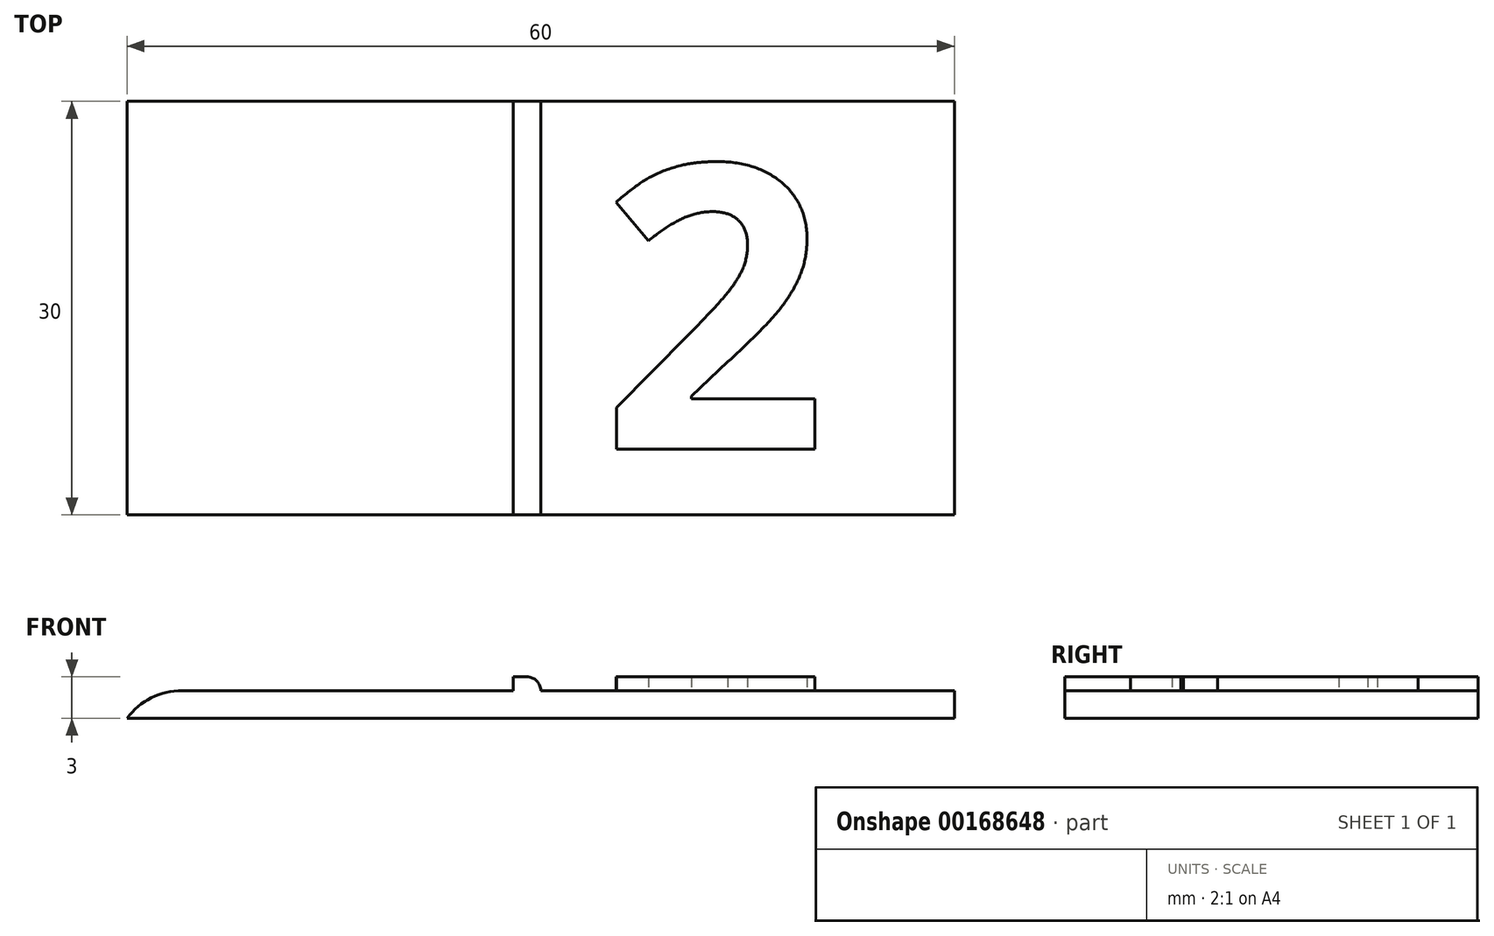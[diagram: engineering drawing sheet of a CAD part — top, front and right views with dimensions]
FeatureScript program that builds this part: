
annotation { "Feature Type Name" : "Feature", "Feature Type Description" : "" }
export const myFeature = defineFeature(function(context is Context, id is Id, definition is map)
    precondition{}
    {
        {
            var Q0;
            Q0=qCreatedBy(makeId("Top.planeOp"),FACE);
            var sketch = newSketch(context, id + "F0", { "sketchPlane" : qUnion([Q0])});
            skLineSegment(sketch, "E0.bottom", {"start": v(0, 0) * mm, "end": v(60, 0) * mm});
            skLineSegment(sketch, "E0.top", {"start": v(0, 30) * mm, "end": v(60, 30) * mm});
            skLineSegment(sketch, "E0.left", {"start": v(0, 0) * mm, "end": v(0, 30) * mm});
            skLineSegment(sketch, "E0.right", {"start": v(60, 0) * mm, "end": v(60, 30) * mm});
            skSolve(sketch);
        }
        {
            var Q0;
            Q0 = qSketchRegion(id + "F0", true);
            extrude(context, id + "F1", {"entities" : qUnion([Q0]), "depth" : 2 * mm});
        }
        {
            var Q0;
            Q0=makeQuery(id+"F1.opExtrude","CAP_FACE",FACE,{"disambiguationData":[OSD([sQuery(id+"F0.wireOp",EDGE,"E0.bottom"),sQuery(id+"F0.wireOp",EDGE,"E0.top"),sQuery(id+"F0.wireOp",EDGE,"E0.left"),sQuery(id+"F0.wireOp",EDGE,"E0.right")])],"isStart":false});
            var sketch = newSketch(context, id + "F2", { "sketchPlane" : qUnion([Q0])});
            skLineSegment(sketch, "E1.bottom", {"start": v(30, 30) * mm, "end": v(28, 30) * mm});
            skLineSegment(sketch, "E1.top", {"start": v(30, 0) * mm, "end": v(28, 0) * mm});
            skLineSegment(sketch, "E1.left", {"start": v(30, 30) * mm, "end": v(30, 0) * mm});
            skLineSegment(sketch, "E1.right", {"start": v(28, 30) * mm, "end": v(28, 0) * mm});
            skSolve(sketch);
        }
        {
            var Q0;
            Q0 = qSketchRegion(id + "F2", true);
            extrude(context, id + "F3", {"entities" : qUnion([Q0]), "operationType" : NewBodyOperationType.ADD, "depth" : 1 * mm});
        }
        {
            var Q0;
            Q0=makeQuery(id+"F3.opExtrude","CAP_EDGE",EDGE,{"disambiguationData":[OSD([sQuery(id+"F2.wireOp",EDGE,"E1.left")])],"isStart":false});
            fillet(context, id + "F4", {"entities" : qUnion([Q0]), "radius" : 1 * mm, "tangentPropagation" : true, "allowEdgeOverflow" : false});
        }
        {
            var Q0;
            {var subQ0=sQuery(id+"F0.wireOp",EDGE,"E0.top");var subQ1=sQuery(id+"F0.wireOp",EDGE,"E0.right");var subQ2=sQuery(id+"F0.wireOp",EDGE,"E0.bottom");Q0=makeQuery(id+"F3.boolean.opBoolean","SPLIT",FACE,{"disambiguationData":[TD([makeQuery(id+"F1.opExtrude","SWEPT_FACE",FACE,{"disambiguationData":[OSD([subQ1])]})])],"derivedFrom":makeQuery(id+"F1.opExtrude","CAP_FACE",FACE,{"disambiguationData":[OSD([subQ2,subQ0,sQuery(id+"F0.wireOp",EDGE,"E0.left"),subQ1])],"isStart":false})});}
            var sketch = newSketch(context, id + "F5", { "sketchPlane" : qUnion([Q0])});
            skText(sketch, "E2", { "text": "2", "fontName": "OpenSans-Bold.ttf"});
            const initialGuessF5  = {"E2": [0.03436, 0.00476, 1, 0, 0.02075]};
            skSetInitialGuess(sketch, initialGuessF5);
            skSolve(sketch);
        }
        {
            var Q0;
            Q0 = qSketchRegion(id + "F5", true);
            extrude(context, id + "F6", {"entities" : qUnion([Q0]), "operationType" : NewBodyOperationType.ADD, "depth" : 1 * mm});
        }
        {
            var Q0;
            Q0=makeQuery(id+"F1.opExtrude","CAP_EDGE",EDGE,{"disambiguationData":[OSD([sQuery(id+"F0.wireOp",EDGE,"E0.left")])],"isStart":false});
            fillet(context, id + "F7", {"entities" : qUnion([Q0]), "radius" : 5 * mm, "tangentPropagation" : true, "allowEdgeOverflow" : false});
        }
    });
